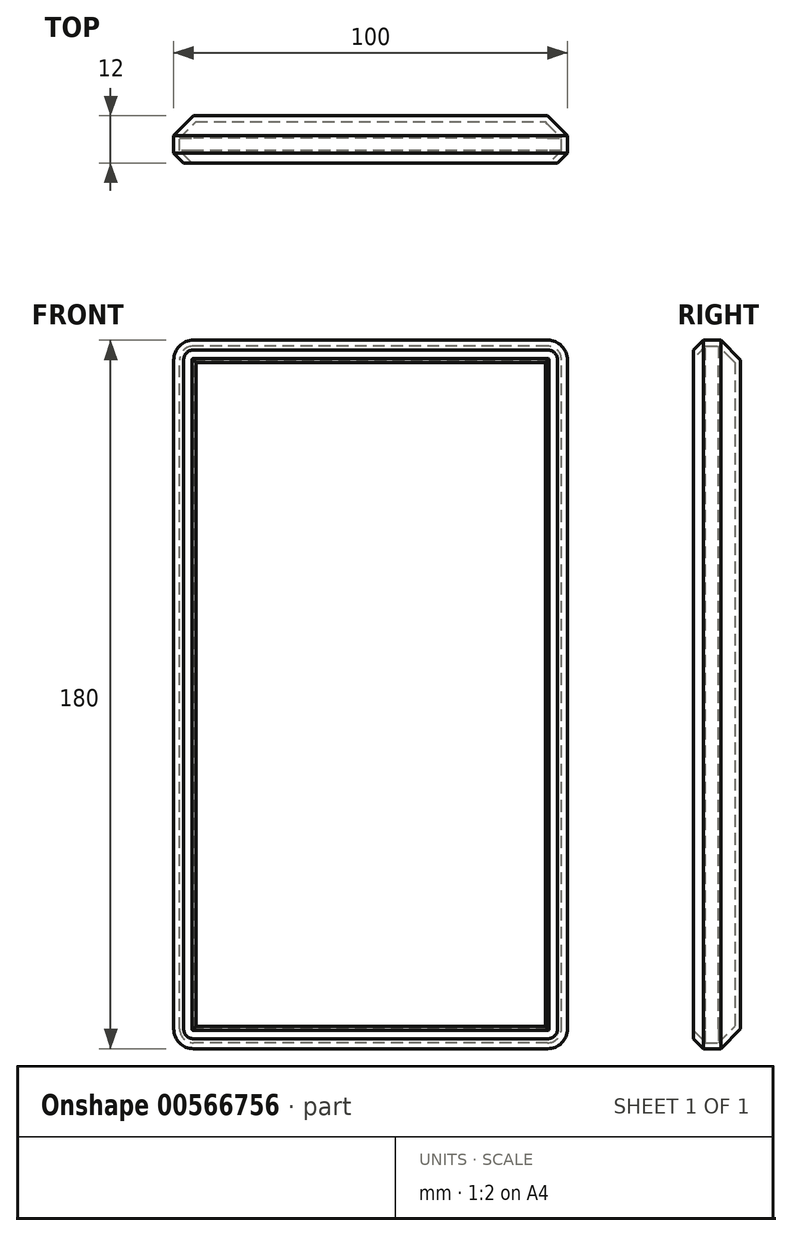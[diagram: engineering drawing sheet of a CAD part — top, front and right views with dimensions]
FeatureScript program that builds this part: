
annotation { "Feature Type Name" : "Feature", "Feature Type Description" : "" }
export const myFeature = defineFeature(function(context is Context, id is Id, definition is map)
    precondition{}
    {
        {
            var Q0;
            Q0=qCreatedBy(makeId("Front.planeOp"),FACE);
            var sketch = newSketch(context, id + "F0", { "sketchPlane" : qUnion([Q0])});
            skLineSegment(sketch, "E0.bottom", {"start": v(0, 0) * mm, "end": v(100, 0) * mm});
            skLineSegment(sketch, "E0.top", {"start": v(0, -180) * mm, "end": v(100, -180) * mm});
            skLineSegment(sketch, "E0.left", {"start": v(0, 0) * mm, "end": v(0, -180) * mm});
            skLineSegment(sketch, "E0.right", {"start": v(100, 0) * mm, "end": v(100, -180) * mm});
            skSolve(sketch);
        }
        {
            var Q0;
            Q0 = qSketchRegion(id + "F0", true);
            extrude(context, id + "F1", {"entities" : qUnion([Q0]), "depth" : 12 * mm, "offsetDistance" : 25 * mm});
        }
        {
            var Q0;
            Q0=makeQuery(id+"F1.opExtrude","SWEPT_EDGE",EDGE,{"disambiguationData":[OSD([sQuery(id+"F0.wireOp",EDGE,"E0.bottom"),sQuery(id+"F0.wireOp",EDGE,"E0.right")])]});
            var Q1;
            Q1=makeQuery(id+"F1.opExtrude","SWEPT_EDGE",EDGE,{"disambiguationData":[OSD([sQuery(id+"F0.wireOp",EDGE,"E0.top"),sQuery(id+"F0.wireOp",EDGE,"E0.right")])]});
            var Q2;
            Q2=makeQuery(id+"F1.opExtrude","SWEPT_EDGE",EDGE,{"disambiguationData":[OSD([sQuery(id+"F0.wireOp",EDGE,"E0.bottom"),sQuery(id+"F0.wireOp",EDGE,"E0.left")])]});
            var Q3;
            Q3=makeQuery(id+"F1.opExtrude","SWEPT_EDGE",EDGE,{"disambiguationData":[OSD([sQuery(id+"F0.wireOp",EDGE,"E0.top"),sQuery(id+"F0.wireOp",EDGE,"E0.left")])]});
            fillet(context, id + "F2", {"entities" : qUnion([Q0, Q1, Q2, Q3]), "radius" : 5 * mm, "tangentPropagation" : true, "allowEdgeOverflow" : false});
        }
        {
            var Q0;
            Q0=makeQuery(id+"F1.opExtrude","CAP_EDGE",EDGE,{"disambiguationData":[OSD([sQuery(id+"F0.wireOp",EDGE,"E0.right")])],"isStart":false});
            var Q1;
            Q1=makeQuery(id+"F1.opExtrude","CAP_EDGE",EDGE,{"disambiguationData":[OSD([sQuery(id+"F0.wireOp",EDGE,"E0.bottom")])],"isStart":false});
            var Q2;
            Q2=makeQuery(id+"F1.opExtrude","CAP_EDGE",EDGE,{"disambiguationData":[OSD([sQuery(id+"F0.wireOp",EDGE,"E0.left")])],"isStart":false});
            var Q3;
            Q3=makeQuery(id+"F1.opExtrude","CAP_EDGE",EDGE,{"disambiguationData":[OSD([sQuery(id+"F0.wireOp",EDGE,"E0.top")])],"isStart":false});
            chamfer(context, id + "F3", {"entities" : qUnion([Q0, Q1, Q2, Q3]), "width" : 2.5 * mm, "tangentPropagation" : true});
        }
        {
            var Q0;
            Q0=makeQuery(id+"F1.opExtrude","CAP_EDGE",EDGE,{"disambiguationData":[OSD([sQuery(id+"F0.wireOp",EDGE,"E0.bottom")])],"isStart":true});
            var Q1;
            {var subQ0=sQuery(id+"F0.wireOp",EDGE,"E0.right");var subQ1=sQuery(id+"F0.wireOp",EDGE,"E0.bottom");Q1=makeQuery(id+"F2.opFillet","BLEND_EDGE",EDGE,{"blendedFrom":[makeQuery(id+"F1.opExtrude","SWEPT_EDGE",EDGE,{"disambiguationData":[OSD([subQ1,subQ0])]}),makeQuery(id+"F1.opExtrude","CAP_FACE",FACE,{"disambiguationData":[OSD([subQ1,sQuery(id+"F0.wireOp",EDGE,"E0.top"),sQuery(id+"F0.wireOp",EDGE,"E0.left"),subQ0])],"isStart":true})],"blendedInto":[makeQuery(id+"F1.opExtrude","CAP_FACE",FACE,{"disambiguationData":[OSD([subQ1,sQuery(id+"F0.wireOp",EDGE,"E0.top"),sQuery(id+"F0.wireOp",EDGE,"E0.left"),subQ0])],"isStart":true})]});}
            var Q2;
            Q2=makeQuery(id+"F1.opExtrude","CAP_EDGE",EDGE,{"disambiguationData":[OSD([sQuery(id+"F0.wireOp",EDGE,"E0.right")])],"isStart":true});
            var Q3;
            {var subQ0=sQuery(id+"F0.wireOp",EDGE,"E0.right");var subQ1=sQuery(id+"F0.wireOp",EDGE,"E0.top");Q3=makeQuery(id+"F2.opFillet","BLEND_EDGE",EDGE,{"blendedFrom":[makeQuery(id+"F1.opExtrude","SWEPT_EDGE",EDGE,{"disambiguationData":[OSD([subQ1,subQ0])]}),makeQuery(id+"F1.opExtrude","CAP_FACE",FACE,{"disambiguationData":[OSD([sQuery(id+"F0.wireOp",EDGE,"E0.bottom"),subQ1,sQuery(id+"F0.wireOp",EDGE,"E0.left"),subQ0])],"isStart":true})],"blendedInto":[makeQuery(id+"F1.opExtrude","CAP_FACE",FACE,{"disambiguationData":[OSD([sQuery(id+"F0.wireOp",EDGE,"E0.bottom"),subQ1,sQuery(id+"F0.wireOp",EDGE,"E0.left"),subQ0])],"isStart":true})]});}
            var Q4;
            Q4=makeQuery(id+"F1.opExtrude","CAP_EDGE",EDGE,{"disambiguationData":[OSD([sQuery(id+"F0.wireOp",EDGE,"E0.top")])],"isStart":true});
            var Q5;
            {var subQ0=sQuery(id+"F0.wireOp",EDGE,"E0.left");var subQ1=sQuery(id+"F0.wireOp",EDGE,"E0.top");Q5=makeQuery(id+"F2.opFillet","BLEND_EDGE",EDGE,{"blendedFrom":[makeQuery(id+"F1.opExtrude","SWEPT_EDGE",EDGE,{"disambiguationData":[OSD([subQ1,subQ0])]}),makeQuery(id+"F1.opExtrude","CAP_FACE",FACE,{"disambiguationData":[OSD([sQuery(id+"F0.wireOp",EDGE,"E0.bottom"),subQ1,subQ0,sQuery(id+"F0.wireOp",EDGE,"E0.right")])],"isStart":true})],"blendedInto":[makeQuery(id+"F1.opExtrude","CAP_FACE",FACE,{"disambiguationData":[OSD([sQuery(id+"F0.wireOp",EDGE,"E0.bottom"),subQ1,subQ0,sQuery(id+"F0.wireOp",EDGE,"E0.right")])],"isStart":true})]});}
            var Q6;
            Q6=makeQuery(id+"F1.opExtrude","CAP_EDGE",EDGE,{"disambiguationData":[OSD([sQuery(id+"F0.wireOp",EDGE,"E0.left")])],"isStart":true});
            var Q7;
            {var subQ0=sQuery(id+"F0.wireOp",EDGE,"E0.left");var subQ1=sQuery(id+"F0.wireOp",EDGE,"E0.bottom");Q7=makeQuery(id+"F2.opFillet","BLEND_EDGE",EDGE,{"blendedFrom":[makeQuery(id+"F1.opExtrude","SWEPT_EDGE",EDGE,{"disambiguationData":[OSD([subQ1,subQ0])]}),makeQuery(id+"F1.opExtrude","CAP_FACE",FACE,{"disambiguationData":[OSD([subQ1,sQuery(id+"F0.wireOp",EDGE,"E0.top"),subQ0,sQuery(id+"F0.wireOp",EDGE,"E0.right")])],"isStart":true})],"blendedInto":[makeQuery(id+"F1.opExtrude","CAP_FACE",FACE,{"disambiguationData":[OSD([subQ1,sQuery(id+"F0.wireOp",EDGE,"E0.top"),subQ0,sQuery(id+"F0.wireOp",EDGE,"E0.right")])],"isStart":true})]});}
            chamfer(context, id + "F4", {"entities" : qUnion([Q0, Q1, Q2, Q3, Q4, Q5, Q6, Q7]), "width" : 5 * mm, "tangentPropagation" : true});
        }
        {
            var Q0;
            Q0=makeQuery(id+"F1.opExtrude","CAP_FACE",FACE,{"disambiguationData":[OSD([sQuery(id+"F0.wireOp",EDGE,"E0.bottom"),sQuery(id+"F0.wireOp",EDGE,"E0.top"),sQuery(id+"F0.wireOp",EDGE,"E0.left"),sQuery(id+"F0.wireOp",EDGE,"E0.right")])],"isStart":false});
            shell(context, id + "F5", {"entities" : qUnion([Q0]), "thickness" : 1.5 * mm});
        }
    });
